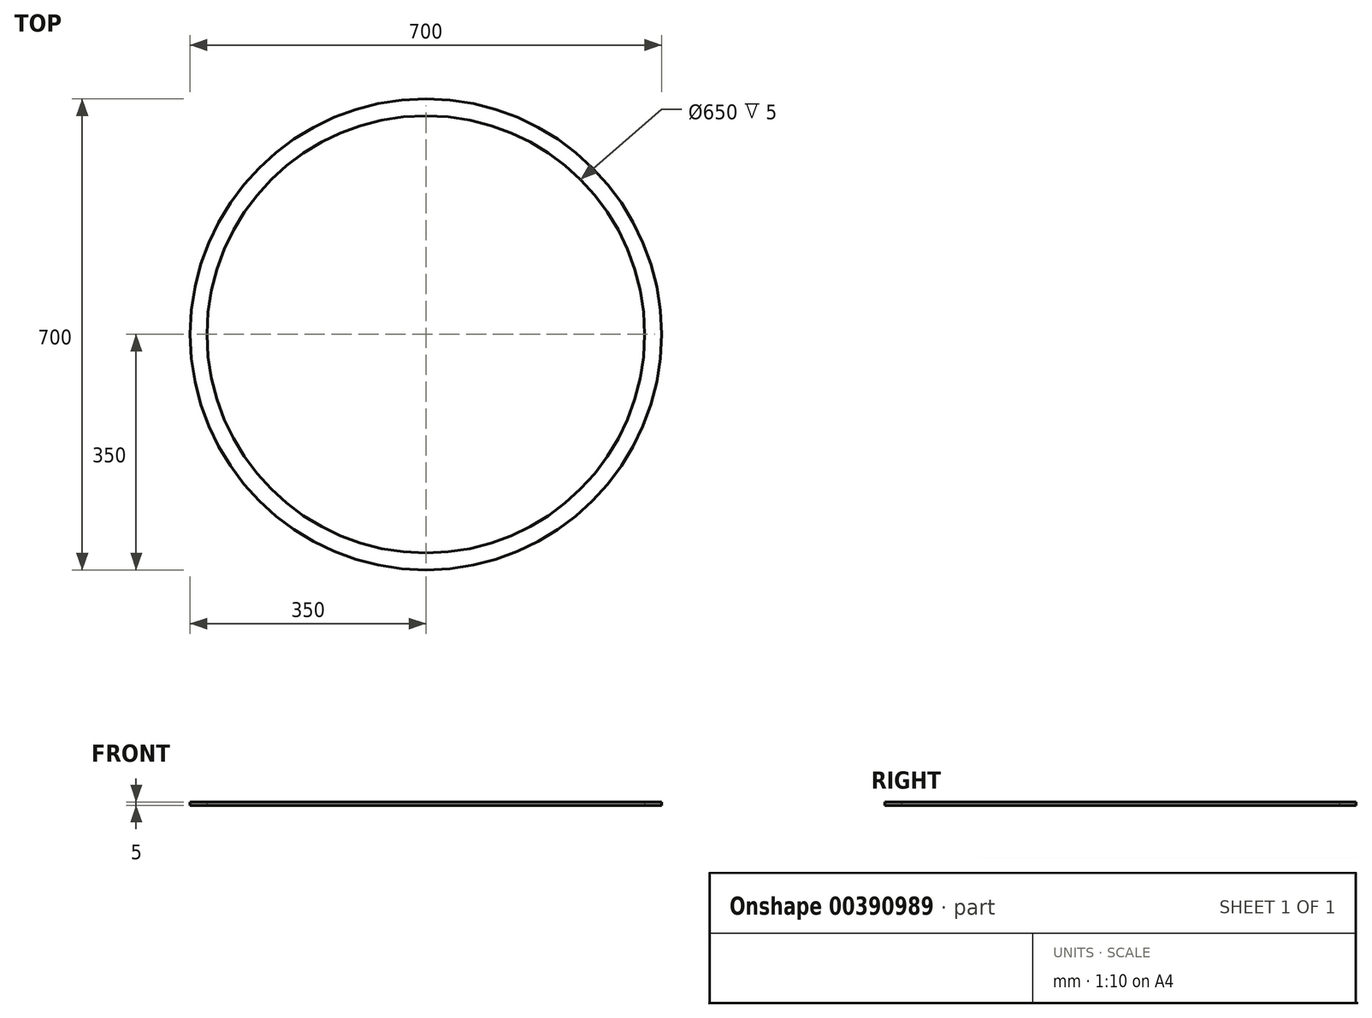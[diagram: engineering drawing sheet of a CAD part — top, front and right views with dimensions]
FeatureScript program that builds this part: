
annotation { "Feature Type Name" : "Feature", "Feature Type Description" : "" }
export const myFeature = defineFeature(function(context is Context, id is Id, definition is map)
    precondition{}
    {
        {
            var Q0;
            Q0=qCreatedBy(makeId("Top.planeOp"),FACE);
            var sketch = newSketch(context, id + "F0", { "sketchPlane" : qUnion([Q0])});
            skCircle(sketch, "E0", {"center": v(0, 0) * mm, "radius": 350 * mm});
            skCircle(sketch, "E1", {"center": v(0, 0) * mm, "radius": 325 * mm});
            skSolve(sketch);
        }
        {
            var Q0;
            Q0=makeQuery(id+"F0.imprint","IMPRINT",FACE,{"disambiguationData":[TD([[makeQuery(id+"F0.imprint","IMPRINT",EDGE,{"derivedFrom":sQuery(id+"F0.wireOp",EDGE,"E0")}),1.0]])]});
            extrude(context, id + "F1", {"entities" : qUnion([Q0]), "depth" : 5 * mm});
        }
    });
